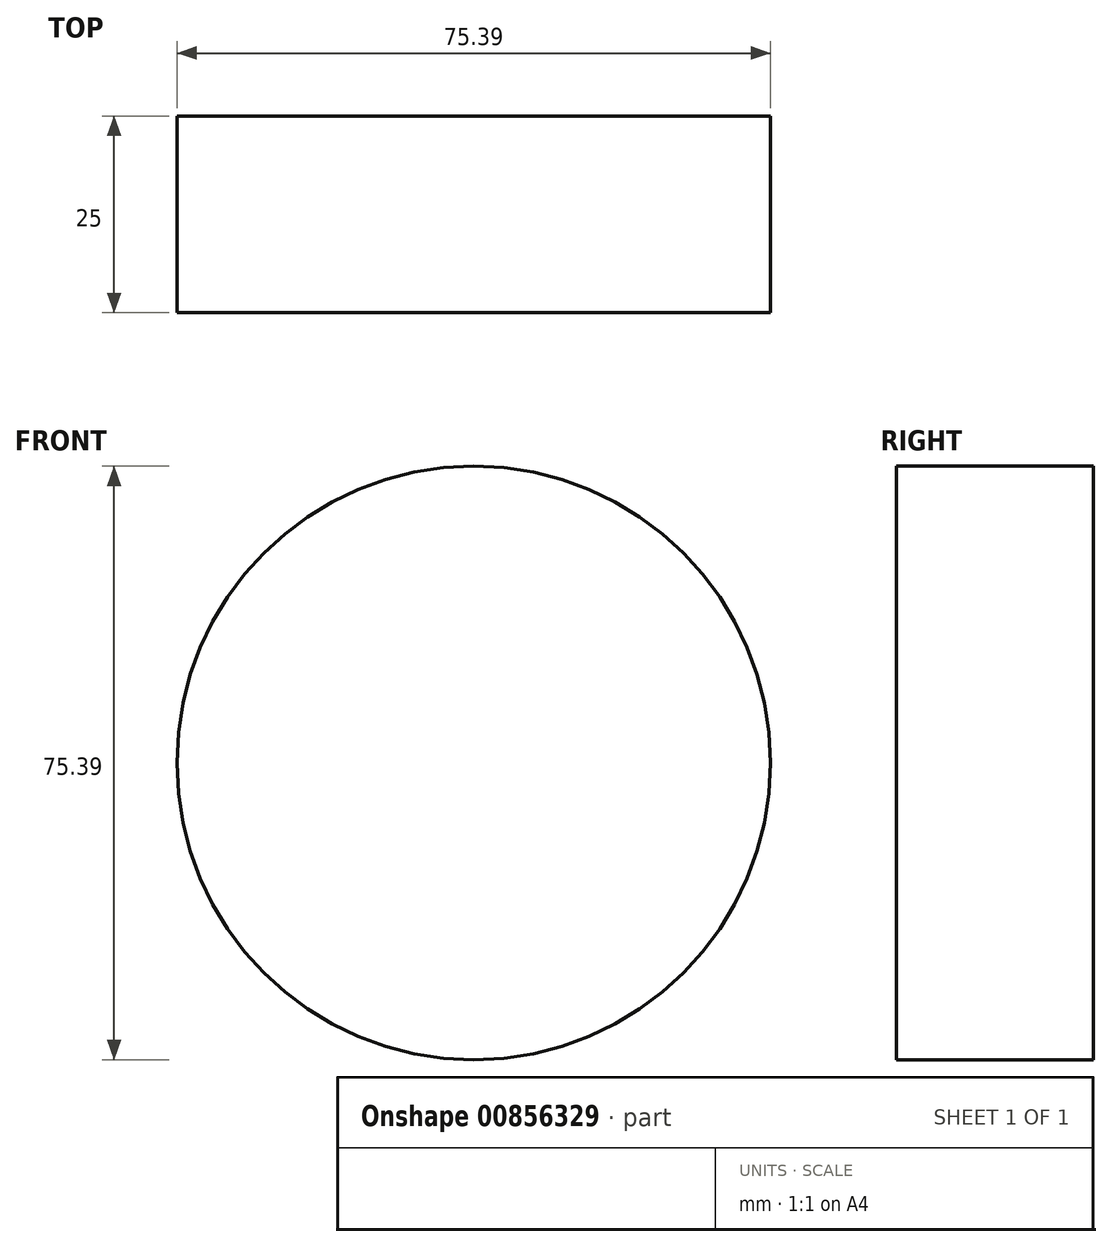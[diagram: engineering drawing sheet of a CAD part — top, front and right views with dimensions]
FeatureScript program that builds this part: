
annotation { "Feature Type Name" : "Feature", "Feature Type Description" : "" }
export const myFeature = defineFeature(function(context is Context, id is Id, definition is map)
    precondition{}
    {
        {
            var Q0;
            Q0=qCreatedBy(makeId("Front.planeOp"),FACE);
            var sketch = newSketch(context, id + "F0", { "sketchPlane" : qUnion([Q0])});
            skCircle(sketch, "E0", {"center": v(-129.6, -17.74) * mm, "radius": 37.7 * mm});
            skSolve(sketch);
        }
        {
            var Q0;
            Q0 = qSketchRegion(id + "F0", true);
            extrude(context, id + "F1", {"entities" : qUnion([Q0]), "depth" : 25 * mm, "offsetDistance" : 25 * mm});
        }
    });
